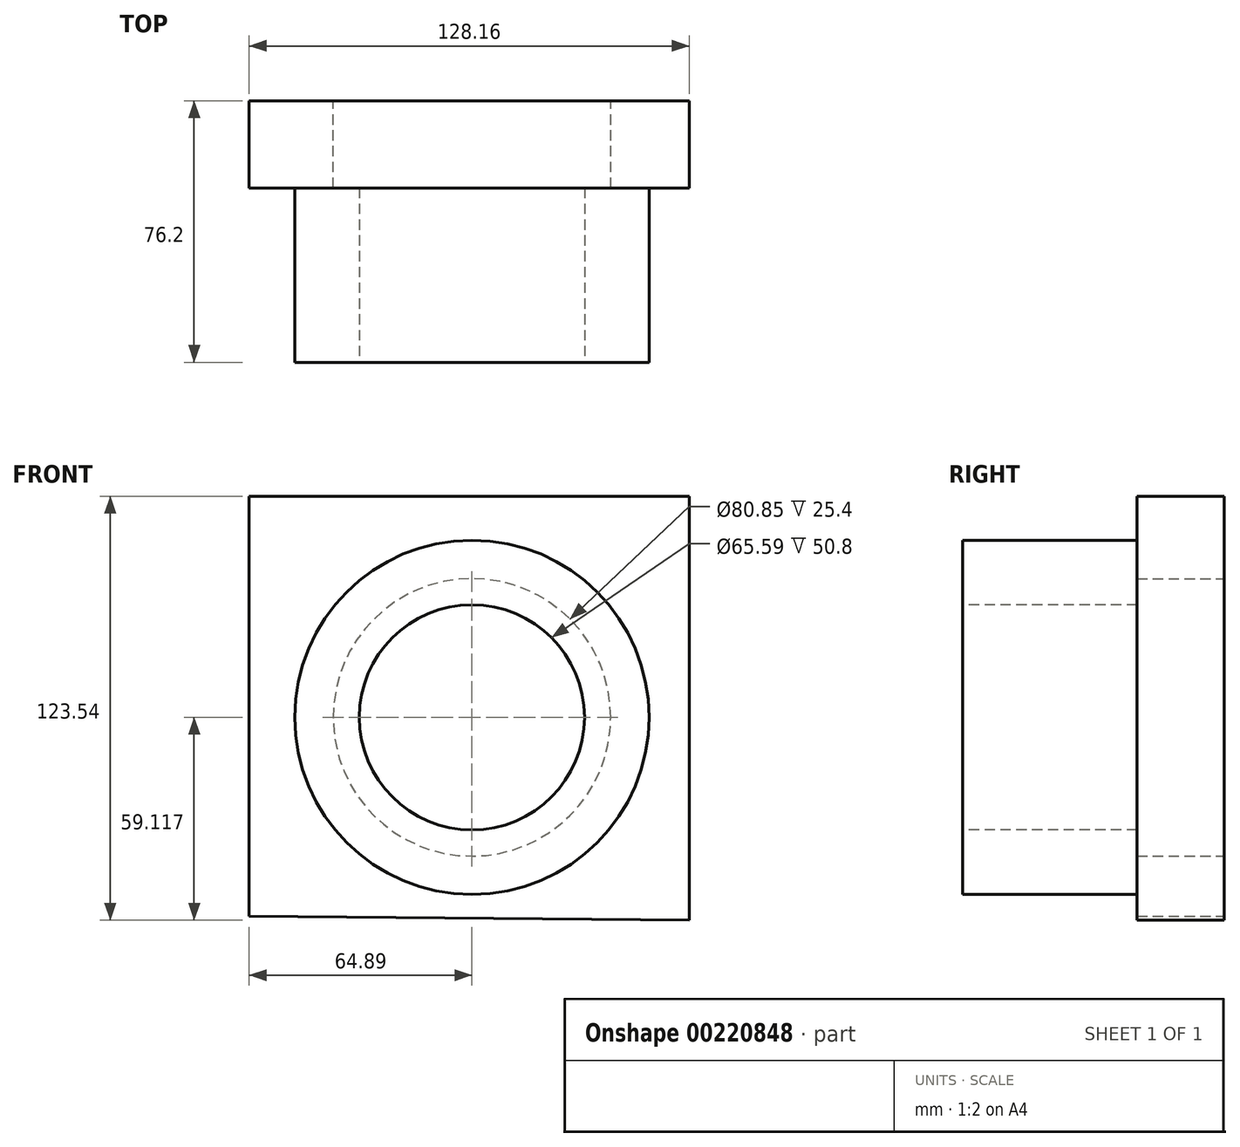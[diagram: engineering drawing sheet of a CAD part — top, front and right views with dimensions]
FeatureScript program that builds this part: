
annotation { "Feature Type Name" : "Feature", "Feature Type Description" : "" }
export const myFeature = defineFeature(function(context is Context, id is Id, definition is map)
    precondition{}
    {
        {
            var Q0;
            Q0=qCreatedBy(makeId("Front.planeOp"),FACE);
            var sketch = newSketch(context, id + "F0", { "sketchPlane" : qUnion([Q0])});
            skLineSegment(sketch, "E0", {"start": v(-64.89, 67.54) * mm, "end": v(-64.89, -54.84) * mm});
            skLineSegment(sketch, "E1", {"start": v(-64.89, 67.54) * mm, "end": v(-64.89, 56) * mm});
            skLineSegment(sketch, "E2", {"start": v(-64.89, 67.54) * mm, "end": v(63.27, 67.54) * mm});
            skLineSegment(sketch, "E3", {"start": v(63.27, 67.54) * mm, "end": v(63.27, -56) * mm});
            skLineSegment(sketch, "E4", {"start": v(63.27, -56) * mm, "end": v(-64.89, -54.84) * mm});
            skSolve(sketch);
        }
        {
            var Q0;
            Q0=makeQuery(id+"F0.imprint","IMPRINT",FACE,{"disambiguationData":[TD([[makeQuery(id+"F0.imprint","IMPRINT",EDGE,{"derivedFrom":sQuery(id+"F0.wireOp",EDGE,"E0")}),1.0]])]});
            var sketch = newSketch(context, id + "F1", { "sketchPlane" : qUnion([Q0])});
            skCircle(sketch, "E5", {"center": v(0, 3.12) * mm, "radius": 40.43 * mm});
            skSolve(sketch);
        }
        {
            var Q0;
            Q0=makeQuery(id+"F1.imprint","IMPRINT",FACE,{"disambiguationData":[TD([[makeQuery(id+"F1.imprint","IMPRINT",EDGE,{"derivedFrom":sQuery(id+"F1.wireOp",EDGE,"E5")}),-1.0]])]});
            extrude(context, id + "F2", {"entities" : qUnion([Q0]), "depth" : 25.4 * mm});
        }
        {
            var Q0;
            Q0=makeQuery(id+"F2.opExtrude","CAP_FACE",FACE,{"disambiguationData":[OSD([sQuery(id+"F0.wireOp",EDGE,"E0"),sQuery(id+"F0.wireOp",EDGE,"E1"),sQuery(id+"F0.wireOp",EDGE,"E2"),sQuery(id+"F0.wireOp",EDGE,"E3"),sQuery(id+"F0.wireOp",EDGE,"E4"),sQuery(id+"F1.wireOp",EDGE,"E5")])],"isStart":false});
            var sketch = newSketch(context, id + "F3", { "sketchPlane" : qUnion([Q0])});
            skCircle(sketch, "E6", {"center": v(0, 3.12) * mm, "radius": 51.6 * mm});
            skSolve(sketch);
        }
        {
            var Q0;
            Q0 = qSketchRegion(id + "F3", true);
            extrude(context, id + "F4", {"entities" : qUnion([Q0]), "operationType" : NewBodyOperationType.ADD, "depth" : 50.8 * mm});
        }
        {
            var Q0;
            Q0=makeQuery(id+"F4.opExtrude","CAP_FACE",FACE,{"disambiguationData":[OSD([sQuery(id+"F3.wireOp",EDGE,"E6")])],"isStart":false});
            var sketch = newSketch(context, id + "F5", { "sketchPlane" : qUnion([Q0])});
            skCircle(sketch, "E7", {"center": v(0, 3.12) * mm, "radius": 32.8 * mm});
            skSolve(sketch);
        }
        {
            var Q0;
            Q0 = qSketchRegion(id + "F5", true);
            extrude(context, id + "F6", {"entities" : qUnion([Q0]), "operationType" : NewBodyOperationType.REMOVE, "oppositeDirection" : true, "depth" : 76.2 * mm});
        }
    });
